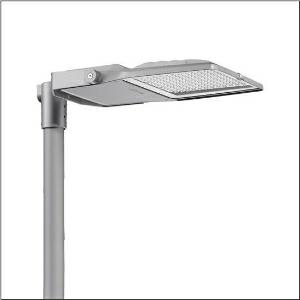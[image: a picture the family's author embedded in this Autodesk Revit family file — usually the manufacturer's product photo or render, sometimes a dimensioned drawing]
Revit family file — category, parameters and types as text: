
# Revit family: floodlight_fl_21_iq_midi___pl52_5xa7781f2d3a_fab9
name_source: partatom
category: Lighting Fixtures
units: mm (PartAtom-declared; Revit-internal decimal feet)

## family parameters
Cut with Voids When Loaded = No
Host = Face
Light Source = No
Part Type = Normal
Room Calculation Point = No
Round Connector Dimension = Use Diameter
Shared = No

## types (1)
- --- (1 x LED, 35760 lm, 270.2 W, 3000K)
    Apparent Load = 270 VA
    CIE Flux Codes = 26 60 98 100 100
    Color Rendering = 70
    Color Temperature = 3000K
    Default Elevation = 1800 mm
    Description = Floodlight FL 21 iQ midi, floodlight, primary light control with lens, of PMMA, primary optical cover: protective disc, of toughened safety glass, transparent, light distribution: PL52, light emission: direct distribution, installation type: surface-mounted, LED, High Power LED, rated luminous flux: 35.760lm, luminous efficacy: 132lm/W, light colour: 730, colour temperature: 3000K, control gear: iQ Comfort/DALI, control: optimised constant luminous flux control (CLO 2.0), Desk-Remote (wireless, voltage-free reading and setting of iQ features in the workshop via application-optimized NFC function/RFID function), Light-Fading, Smart-Wire, Night-Set, Lumen-Switch, Temp-Guard, Auto-Match, with terminal, 6-pole, mains connection: 220..240V, AC, 50/60Hz, start of lifetime: 270W, end of service life: 287W, reduction: 117W, luminaire housing, of diecast aluminium, powder-coated, Siteco® metallic grey (DB 702S), corrosivity category C5 mid according to DIN EN ISO 12944, suitable for swimming pools, chlorine-resistant, sealing non-destructively replaceable, please order mast flange separately, mast bracket, of steel, galvanised, powder-coated, Siteco® metallic grey (DB 702S), protection rating (complete): IP66, insulation class (complete): insulation class II (safety insulation), certification: CE, ENEC, VDE, protection symbol: D, impact resistance: IK08, permissible operating ambient temperature: -40..+40°C, permissible operating ambient temperature for outdoor applications: -40..+50°C, standard: DIN EN 12944, LABS conformity tested according to VDMA 24364:2018-05, packaging unit: 1 piece

Light Distribution: PL52
    Height = 76 mm
    Lamp = 1 x LED
    Lamp Light Flux = 35760 lm
    Lamp Power = 270.2 W
    Lamp count = 1
    Length = 657 mm
    Luminous efficacy = 132 lm/W
    Manufacturer = Siteco
    ModVariant = No
    Model = 5XA7781F2D3A
    Number of Poles = 1
    OnlyDefault = Yes
    Power Factor = 1
    Product Name = Floodlight FL 21 iQ midi | PL52
    Product group = floodlight | pylon annexe
    ProductGroupID = 6200
    Protection Class = Protection class II
    Protection Degree = IP 66
    RLX_Detail_Level = 1
    RLX_Emergency_Light_Flux = 0 lm
    RLX_Emergency_Type = 0
    RLX_Emergency_Type_DB = No
    RlxData = <blob elided: 153829 chars, md5=33e36c35>
    Socket = socket
    Standby Power = 0 W
    System Light Flux = 35760 lm
    System Power = 270 W
    Type Comments = factory setting: luminous flux: 100 % | dim-lin: 254 | 620 mA
    Type Image = l_1007123.jpg
    URL = http://relux.com
    VarID = @adj_105826
    Voltage = 0 V
    Weight = 0.00 kg
    Width = 442 mm

## geometry (parser evidence)
native form markers: Blend x4, Sweep x15
no freeform markers — native parametric forms only
